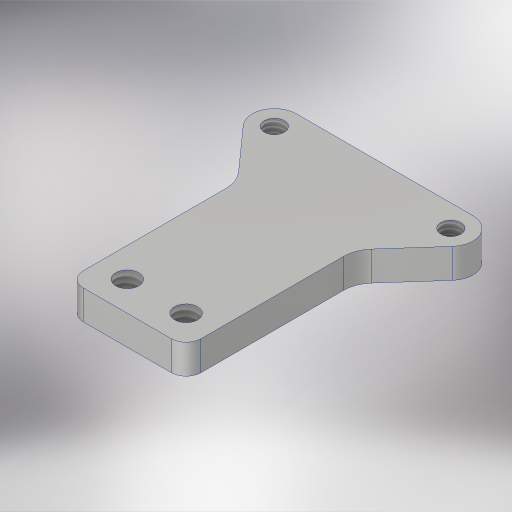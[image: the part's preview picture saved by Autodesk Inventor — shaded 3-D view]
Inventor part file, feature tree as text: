
AUTODESK INVENTOR PART (.ipt)
format: ipt  version: 2023.4 (Build 274418000, 418)  size: 599,040 bytes
history: native  units: in
note: dims shown in document units (in); Inventor stores cm internally (conversion verified against a paired STEP export)
features: other x7, fillet x5, extrude x4, sketch x3, hole x2, projected_geometry x1
ambient origin geometry x8: Origin, YZ Plane, XZ Plane, XY Plane, X Axis, Y Axis, Z Axis, Center Point
bodies: Solid1 (feature_tree)
feature tree (22):
  sketch  "Sketch1"  dims[d1=0.7in d3=0.13in]
  extrude  "Extrusion1"  Depth=0.13in
  hole  "Hole1"  [1 undecoded]
  fillet  "Fillet1"  Radius=1.0in
  extrude  "Extrusion2"  Depth=0.0625in
  other  "Full Round Fillet1"
  other  "Full Round Fillet2"
  other  "Full Round Fillet3"
  other  "Full Round Fillet4"
  other  "Full Round Fillet5"
  other  "Full Round Fillet6"
  other  "Full Round Fillet7"
  fillet  "Fillet3"  Radius=0.5in
  sketch  "Sketch4"  dims[d4=0.197in d5=0.197in d8=1.0in]
  extrude  "Extrusion5"  Depth=0.0625in
  hole  "Hole2"  [1 undecoded]
  extrude  "Extrusion6"  Depth=0.0625in
  fillet  "Fillet4"  Radius=0.3937in
  fillet  "Fillet5"  Radius=0.3937in
  fillet  "Fillet6"  Radius=0.17in
  sketch  "Sketch5"  dims[d9=2.0in d10=0.25in d11=0.5in d12=0.25in d13=0.25in d14=0.0in d15=0.196in d16=0.5in d17=0.385in d18=0.25in d19=0.5635in d20=1.0in d21=0.8108in d22=0.125in d23=0.7874in d25=0.197in d26=0.3937in d28=1.0in d30=1.5748in d32=0.197in d33=0.3937in d35=1.0in d37=0.17in d38=0.0in d43=0.0625in d50=1.5in d51=0.375in d52=0.75in d53=1.0in d54=0.0in d55=0.171in d56=0.432in d57=0.385in d58=0.25in d59=0.5635in d60=1.0in d61=0.8108in d62=0.125in d63=0.06in d64=0.0in d65=0.26in d66=0.13in d67=0.0625in]
  projected_geometry  "Project Cut Edges2"
note: 2 required parameter values undecoded (feature->parameter linkage not recoverable at this tier; creation-order binding heuristic only, values carry confidence <= 0.55)
